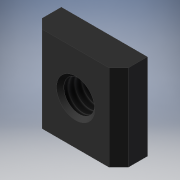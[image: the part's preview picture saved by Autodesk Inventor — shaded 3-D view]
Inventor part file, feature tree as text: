
AUTODESK INVENTOR PART (.ipt)
format: ipt  version: 2019 (Build 230136000, 136)  size: 126,464 bytes
history: native  units: mm
features: sketch x3, extrude x2, revolve x1, thread x1
ambient origin geometry x8: Origin, YZ Plane, XZ Plane, XY Plane, X Axis, Y Axis, Z Axis, Center Point
bodies: Solid1 (feature_tree)
feature tree (7):
  extrude  "Extrusion1"  TaperAngle=360.0deg  [1 undecoded]
  revolve  "Revolution1"  [1 undecoded]
  thread  "Thread1"  [1 undecoded]
  extrude  "Extrusion2"  [1 undecoded]
  sketch  "Sketch_1"  dims[d0=3.0mm d1=0.0mm d2=360.0deg]
  sketch  "Sketch_2"  dims[d3=2.242mm d4=0.0mm d5=18.0mm d6=0.0mm]
  sketch  "Sketch_3"
note: 4 required parameter values undecoded (feature->parameter linkage not recoverable at this tier; creation-order binding heuristic only, values carry confidence <= 0.55)